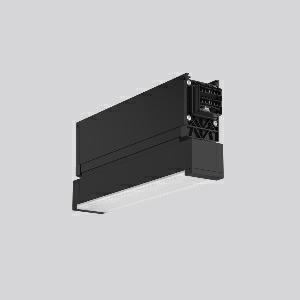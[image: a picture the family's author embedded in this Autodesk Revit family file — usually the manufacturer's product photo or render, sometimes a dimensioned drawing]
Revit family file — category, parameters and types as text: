
# Revit family: linedo_module_rw_9503rw_763_409_0hc_eceb
name_source: partatom
category: Lighting Fixtures
units: mm (PartAtom-declared; Revit-internal decimal feet)

## family parameters
Cut with Voids When Loaded = No
Host = Face
Light Source = No
Part Type = Normal
Room Calculation Point = No
Round Connector Dimension = Use Diameter
Shared = No

## types (1)
- LINEDO Module RW (1 x LED Modul 763, 340 lm, 6300)
    Apparent Load = 7 VA
    CIE Flux Codes = 36 68 94 98 100
    Color Rendering = 70
    Color Temperature = 6300
    Default Elevation = 1800 mm
    Description = LINEDO, 6,5 W, 340 lm, 763, black, on/off
Continuous line luminaire, L 342 B 58 H 147, CBS, emergency-340 lm, AC-Control
Project solution!
    Height = 147 mm
    Lamp = 1 x LED Modul 763
    Lamp Light Flux = 340 lm
    Lamp count = 1
    Length = 342 mm
    Lifetime = 50000 h
    Luminous efficacy = 52 lm/W
    Manufacturer = RZB
    ModVariant = No
    Model = 9503RW.763.409.0HC
    Mounting Place = Ceiling
    Mounting Type = Surface mounted
    Number of Poles = 1
    OnlyDefault = Yes
    Power Factor = 1
    Product Name = LINEDO Module RW
    Product group = Surface mounted continuous line luminaire system
    ProductGroupID = 310
    Protection Class = Protection class I
    Protection Degree = IP 54
    RLX_Detail_Level = 1
    RLX_Emergency_Light_Flux = 340 lm
    RLX_Emergency_Type = 3
    RLX_Emergency_Type_DB = Yes
    RlxData = <blob elided: 35685 chars, md5=41886b39>
    Socket = socket
    Standby Power = 0 W
    System Light Flux = 340 lm
    System Power = 7 W
    Type Comments = Product without accessories
    Type Image = 9503rf.763.430.0hc.jpg
    URL = http://relux.com
    VarID = ---
    Voltage = 230 V
    Voltage Range = 220-240 V
    Weight = 0.00 kg
    Width = 58 mm

## geometry (parser evidence)
native form markers: Blend x4, Sweep x11
no freeform markers — native parametric forms only
